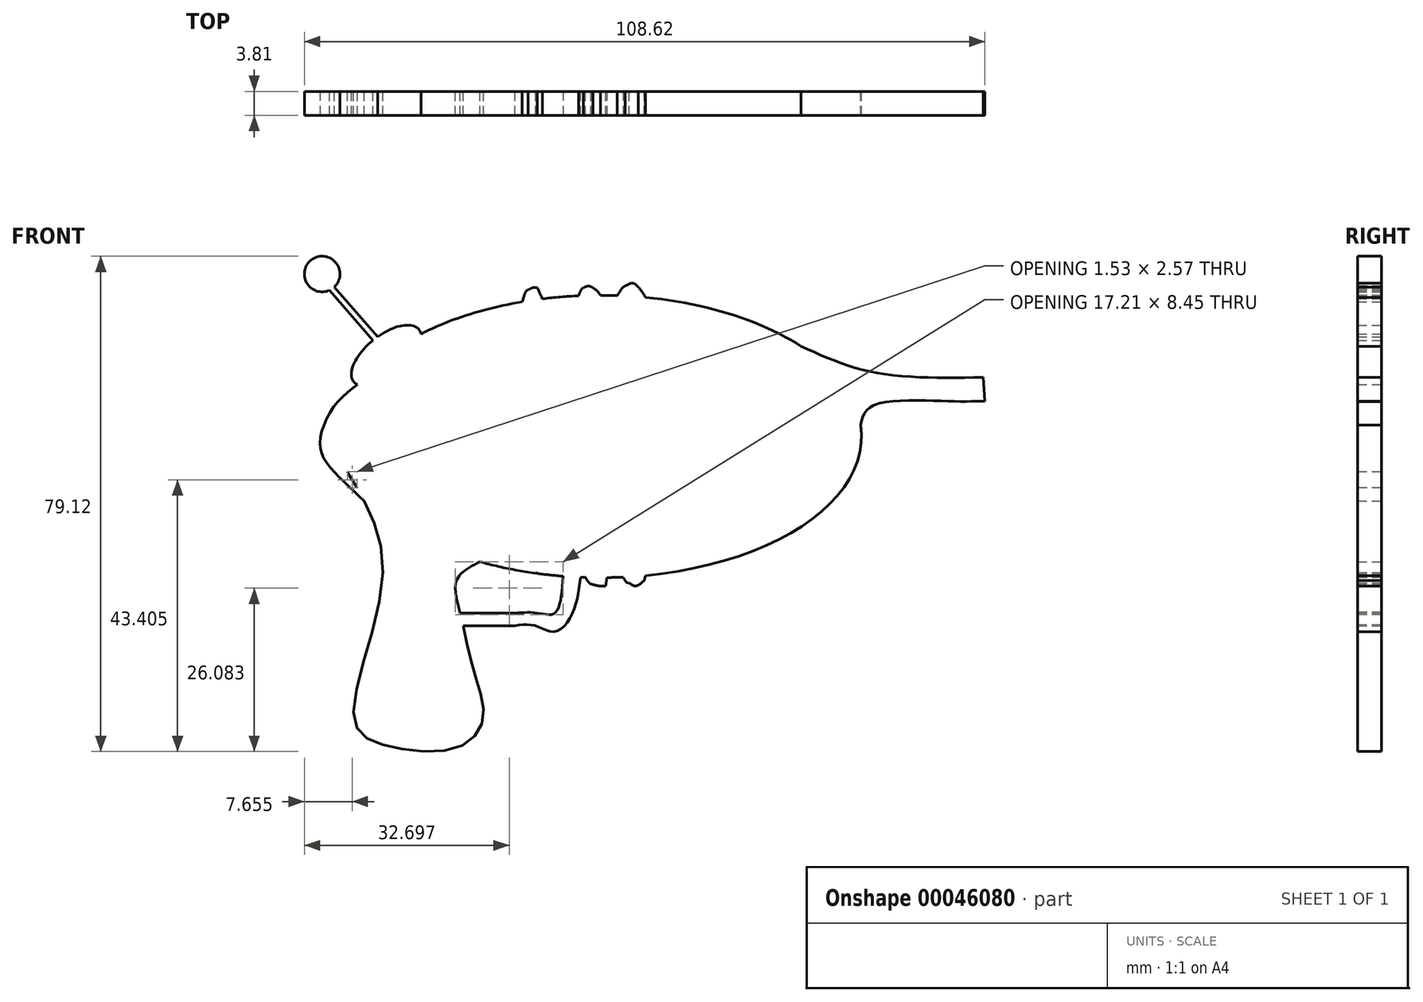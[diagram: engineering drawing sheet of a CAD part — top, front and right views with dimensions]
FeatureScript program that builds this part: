
annotation { "Feature Type Name" : "Feature", "Feature Type Description" : "" }
export const myFeature = defineFeature(function(context is Context, id is Id, definition is map)
    precondition{}
    {
        {
            var Q0;
            Q0=qCreatedBy(makeId("Front.planeOp"),FACE);
            var sketch = newSketch(context, id + "F0", { "sketchPlane" : qUnion([Q0])});
            skEllipse(sketch, "E0", {"center": v(0, 0) * mm, "majorRadius": 41.67 * mm, "minorRadius": 22.55 * mm, "majorAxis": v(1, 0)});
            skFitSpline(sketch, "E1", {"points": [v(-40.35, -5.63) * mm, v(-34.74, -22.23) * mm, v(-39.36, -44.93) * mm, v(-34.6, -49.28) * mm, v(-22.5, -49.56) * mm, v(-18.7, -44.8) * mm, v(-20.19, -37.46) * mm, v(-22.36, -28.21) * mm, v(-22.9, -22.9) * mm, v(-19.22, -20.01) * mm], "startDerivative": vector(59.42, -98.15) * mm, "endDerivative": vector(60.59, 31.88) * mm});
            skLineSegment(sketch, "E2", {"start": v(-22.36, -28.21) * mm, "end": v(-13.63, -28.21) * mm});
            skLineSegment(sketch, "E3", {"start": v(-21.9, -30.24) * mm, "end": v(-13.63, -30.24) * mm});
            skFitSpline(sketch, "E4", {"points": [v(-13.63, -28.21) * mm, v(-10, -28.21) * mm, v(-7.27, -28.21) * mm, v(-5.94, -22.32) * mm], "startDerivative": vector(11.53, 0.81) * mm, "endDerivative": vector(1.3, 18.85) * mm});
            skFitSpline(sketch, "E5", {"points": [v(-13.63, -30.24) * mm, v(-10.37, -30.24) * mm, v(-7.27, -31.2) * mm, v(-4.42, -28.21) * mm, v(-3.16, -22.49) * mm], "startDerivative": vector(14.6, 2.11) * mm, "endDerivative": vector(2.28, 19.94) * mm});
            skFitSpline(sketch, "E6", {"points": [v(-17.45, -20.48) * mm, v(-18.33, -22.78) * mm, v(-16.62, -26.55) * mm, v(-16.38, -26.55) * mm], "startDerivative": vector(-3.85, -4.93) * mm, "endDerivative": vector(1.7, 0.89) * mm});
            skFitSpline(sketch, "E7", {"points": [v(-15.93, -20.84) * mm, v(-16.13, -22.53) * mm, v(-16.38, -26.55) * mm], "startDerivative": vector(-0.55, -3.83) * mm, "endDerivative": vector(-0.36, -7.35) * mm});
            skEllipse(sketch, "E8", {"center": v(-34.16, 12.92) * mm, "majorRadius": 6.67 * mm, "minorRadius": 3.24 * mm, "majorAxis": v(0.78, 0.62)});
            skLineSegment(sketch, "E9", {"start": v(-34.16, 12.92) * mm, "end": v(-43.67, 23.88) * mm});
            skLineSegment(sketch, "E10", {"start": v(-42.45, 23.88) * mm, "end": v(-33.42, 13.47) * mm});
            skLineSegment(sketch, "E11", {"start": v(-33.42, 13.47) * mm, "end": v(-33.31, 14.26) * mm});
            skCircle(sketch, "E12", {"center": v(-44.4, 25.95) * mm, "radius": 2.84 * mm});
            skFitSpline(sketch, "E13", {"points": [v(-38.76, 8.28) * mm, v(-36.24, 3.17) * mm, v(-35.38, -4.62) * mm, v(-37.37, -10.56) * mm], "startDerivative": vector(9.01, -15.02) * mm, "endDerivative": vector(-7.85, -17.1) * mm});
            skFitSpline(sketch, "E14", {"points": [v(-37.37, -10.56) * mm, v(-41.47, -6.7) * mm, v(-44.28, -3.16) * mm, v(-44.64, 0) * mm, v(-42.45, 4.88) * mm, v(-38.76, 8.28) * mm], "startDerivative": vector(-19.21, 17.5) * mm, "endDerivative": vector(19.08, 14.48) * mm});
            skFitSpline(sketch, "E15", {"points": [v(-12.46, 21.52) * mm, v(-11.5, 23.4) * mm, v(-8.22, 10) * mm, v(-6.88, -4.75) * mm, v(-8.22, -19.85) * mm, v(-9.13, -22) * mm, v(-9.95, -21.9) * mm, v(-10.35, -21.85) * mm, v(-9.07, -23.5) * mm, v(-5.94, -19.85) * mm, v(-3.83, -4.62) * mm, v(-5.05, 10.48) * mm, v(-10.04, 23.76) * mm], "startDerivative": vector(18.77, 64.42) * mm, "endDerivative": vector(-48.51, 107.98) * mm});
            skFitSpline(sketch, "E16", {"points": [v(-11.5, 23.4) * mm, v(-10.75, 23.78) * mm, v(-10.04, 23.76) * mm], "startDerivative": vector(1.43, 0.93) * mm, "endDerivative": vector(1.5, -0.22) * mm});
            skPoint(sketch, "E17.3.internal.snap0", {"position": v(0, 22.55) * mm});
            skFitSpline(sketch, "E17", {"points": [v(-3.46, 22.47) * mm, v(-2.7, 23.76) * mm, v(-1.52, 22.54) * mm, v(0, 10.9) * mm, v(0, -4.6) * mm, v(-1.19, -22.54) * mm, v(-1.52, -23.57) * mm, v(-2.37, -22.52) * mm], "startDerivative": vector(8.42, 24.9) * mm, "endDerivative": vector(-13.5, 22.51) * mm});
            skFitSpline(sketch, "E18", {"points": [v(-1.18, 23.76) * mm, v(0, 22.55) * mm, v(2.46, 11.31) * mm, v(3.05, -4.62) * mm, v(0.85, -23.9) * mm], "startDerivative": vector(12.07, -7.71) * mm, "endDerivative": vector(-8.38, -58.92) * mm});
            skFitSpline(sketch, "E19", {"points": [v(-1.52, -23.57) * mm, v(0, -23.9) * mm, v(0.85, -23.9) * mm], "startDerivative": vector(2.83, -0.76) * mm, "endDerivative": vector(1.86, 0.12) * mm});
            skFitSpline(sketch, "E20", {"points": [v(-2.7, 23.76) * mm, v(-1.83, 24.03) * mm, v(-1.18, 23.76) * mm], "startDerivative": vector(1.7, 0.8) * mm, "endDerivative": vector(1.34, -0.82) * mm});
            skFitSpline(sketch, "E21", {"points": [v(2.72, 22.5) * mm, v(4, 24.03) * mm, v(5.16, 22.38) * mm, v(8.48, 10.18) * mm, v(7.67, -6.72) * mm, v(4.57, -23.4) * mm, v(3.64, -22.47) * mm], "startDerivative": vector(14.73, 25.68) * mm, "endDerivative": vector(-12.6, 23.08) * mm});
            skFitSpline(sketch, "E22", {"points": [v(6.06, 23.86) * mm, v(7.22, 22.21) * mm, v(10.78, 10.53) * mm, v(10.32, -7.18) * mm, v(6.98, -23.03) * mm], "startDerivative": vector(9.74, -11.4) * mm, "endDerivative": vector(-12.16, -50.74) * mm});
            skFitSpline(sketch, "E23", {"points": [v(4.57, -23.4) * mm, v(5.66, -23.87) * mm, v(6.98, -23.03) * mm], "startDerivative": vector(2.3, -1.63) * mm, "endDerivative": vector(2.51, 2.28) * mm});
            skFitSpline(sketch, "E24", {"points": [v(4, 24.03) * mm, v(5.16, 24.48) * mm, v(6.06, 23.86) * mm], "startDerivative": vector(2.34, 1.28) * mm, "endDerivative": vector(1.8, -1.65) * mm});
            skFitSpline(sketch, "E25", {"points": [v(32.03, 14.42) * mm, v(43.57, 10.26) * mm, v(61.11, 9.45) * mm], "startDerivative": vector(23.83, -10.8) * mm, "endDerivative": vector(34.06, 0.57) * mm});
            skFitSpline(sketch, "E26", {"points": [v(41.53, 1.84) * mm, v(43.3, 4.83) * mm, v(55.13, 5.64) * mm, v(61.38, 5.64) * mm], "startDerivative": vector(3.27, 14.5) * mm, "endDerivative": vector(16.38, 0.37) * mm});
            skLineSegment(sketch, "E27", {"start": v(61.11, 9.45) * mm, "end": v(61.38, 5.64) * mm});
            skSolve(sketch);
        }
        {
            var Q0;
            Q0 = qSketchRegion(id + "F0", true);
            extrude(context, id + "F1", {"entities" : qUnion([Q0]), "depth" : 3.8 * mm});
        }
    });
